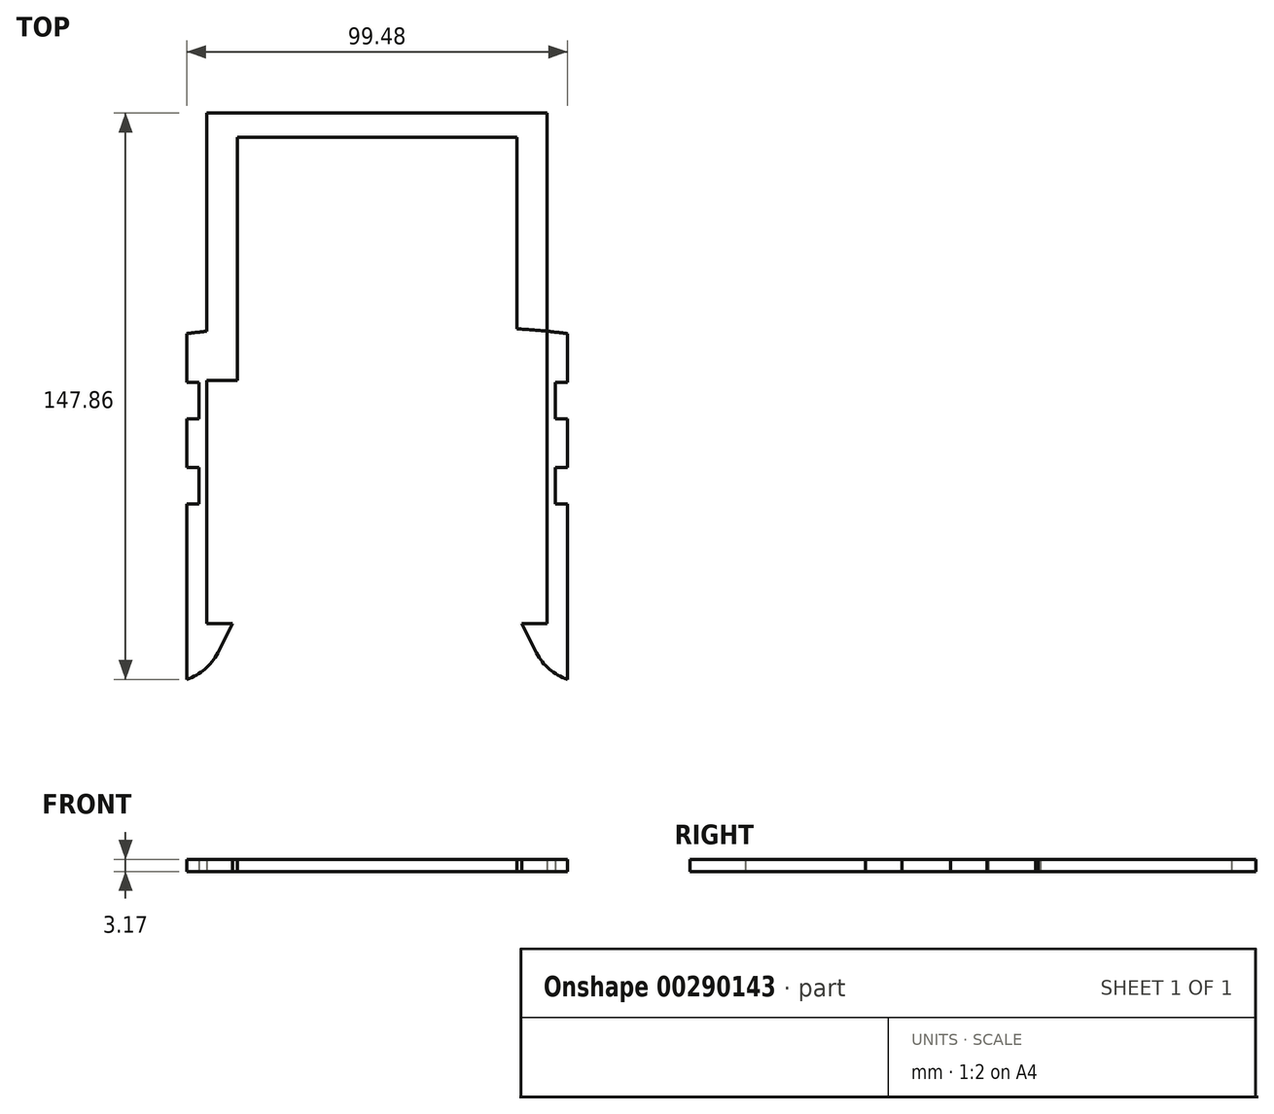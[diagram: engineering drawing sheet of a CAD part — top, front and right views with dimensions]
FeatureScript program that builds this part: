
annotation { "Feature Type Name" : "Feature", "Feature Type Description" : "" }
export const myFeature = defineFeature(function(context is Context, id is Id, definition is map)
    precondition{}
    {
        {
            var Q0;
            Q0=qCreatedBy(makeId("Top.planeOp"),FACE);
            var sketch = newSketch(context, id + "F0", { "sketchPlane" : qUnion([Q0])});
            skLineSegment(sketch, "E0", {"start": v(0, 51.86) * mm, "end": v(-27.09, 51.86) * mm});
            skLineSegment(sketch, "E1", {"start": v(0, -7.34) * mm, "end": v(-21.95, -7.34) * mm});
            skLineSegment(sketch, "E2", {"start": v(-31.65, -13.33) * mm, "end": v(-41.64, -33.02) * mm});
            skArc(sketch, "E3", {"start": v(-21.95, -7.34) * mm, "mid": v(-27.65, -8.97) * mm, "end": v(-31.65, -13.33) * mm});
            skArc(sketch, "E4", {"start": v(-59.94, -39.17) * mm, "mid": v(-49.53, -39.84) * mm, "end": v(-41.64, -33.02) * mm});
            skArc(sketch, "E5", {"start": v(-76.83, -17.66) * mm, "mid": v(-71.66, -30.99) * mm, "end": v(-59.94, -39.17) * mm});
            skArc(sketch, "E6", {"start": v(-58.6, 46.17) * mm, "mid": v(-70.66, 15.1) * mm, "end": v(-76.83, -17.66) * mm});
            skArc(sketch, "E7", {"start": v(-49.74, 50.36) * mm, "mid": v(-54.5, 48.95) * mm, "end": v(-58.6, 46.17) * mm});
            skArc(sketch, "E8", {"start": v(-27.09, 51.86) * mm, "mid": v(-38.44, 51.49) * mm, "end": v(-49.74, 50.36) * mm});
            skArc(sketch, "E9.MirrorCS", {"start": v(27.09, 51.86) * mm, "mid": v(38.44, 51.49) * mm, "end": v(49.74, 50.36) * mm});
            skArc(sketch, "E10.MirrorCS", {"start": v(49.74, 50.36) * mm, "mid": v(54.5, 48.95) * mm, "end": v(58.6, 46.17) * mm});
            skArc(sketch, "E11.MirrorCS", {"start": v(21.95, -7.34) * mm, "mid": v(27.65, -8.97) * mm, "end": v(31.65, -13.33) * mm});
            skLineSegment(sketch, "E12.MirrorCS", {"start": v(0, -7.34) * mm, "end": v(21.95, -7.34) * mm});
            skArc(sketch, "E13.MirrorCS", {"start": v(59.94, -39.17) * mm, "mid": v(49.53, -39.84) * mm, "end": v(41.64, -33.02) * mm});
            skArc(sketch, "E14.MirrorCS", {"start": v(76.83, -17.66) * mm, "mid": v(71.66, -30.99) * mm, "end": v(59.94, -39.17) * mm});
            skArc(sketch, "E15.MirrorCS", {"start": v(58.6, 46.17) * mm, "mid": v(70.66, 15.1) * mm, "end": v(76.83, -17.66) * mm});
            skLineSegment(sketch, "E16.MirrorCS", {"start": v(0, 51.86) * mm, "end": v(27.09, 51.86) * mm});
            skLineSegment(sketch, "E17.MirrorCS", {"start": v(31.65, -13.33) * mm, "end": v(41.64, -33.02) * mm});
            skLineSegment(sketch, "E18.bottom", {"start": v(-36.51, 101.6) * mm, "end": v(36.51, 101.6) * mm});
            skLineSegment(sketch, "E18.top", {"start": v(-36.51, 38.1) * mm, "end": v(36.51, 38.1) * mm});
            skLineSegment(sketch, "E18.left", {"start": v(-36.51, 101.6) * mm, "end": v(-36.51, 38.1) * mm});
            skLineSegment(sketch, "E18.right", {"start": v(36.51, 101.6) * mm, "end": v(36.51, 38.1) * mm});
            skPoint(sketch, "E18.middle", {"position": v(0, 69.85) * mm});
            skLineSegment(sketch, "E19.bottom", {"start": v(-44.45, -25.4) * mm, "end": v(44.45, -25.4) * mm});
            skLineSegment(sketch, "E19.top", {"start": v(-44.45, 38.1) * mm, "end": v(44.45, 38.1) * mm});
            skLineSegment(sketch, "E19.left", {"start": v(-44.45, -25.4) * mm, "end": v(-44.45, 38.1) * mm});
            skLineSegment(sketch, "E19.right", {"start": v(44.45, -25.4) * mm, "end": v(44.45, 38.1) * mm});
            skPoint(sketch, "E19.middle", {"position": v(0, 6.35) * mm});
            skLineSegment(sketch, "E20", {"start": v(-44.45, 38.1) * mm, "end": v(-44.45, 107.95) * mm});
            skLineSegment(sketch, "E21", {"start": v(-44.45, 107.95) * mm, "end": v(44.45, 107.95) * mm});
            skLineSegment(sketch, "E22", {"start": v(44.45, 107.95) * mm, "end": v(44.45, 38.1) * mm});
            skLineSegment(sketch, "E23.bottom", {"start": v(-49.74, 37.66) * mm, "end": v(-46.56, 37.66) * mm});
            skLineSegment(sketch, "E23.top", {"start": v(-49.74, 28.13) * mm, "end": v(-46.56, 28.13) * mm});
            skLineSegment(sketch, "E23.left", {"start": v(-49.74, 37.66) * mm, "end": v(-49.74, 28.13) * mm});
            skLineSegment(sketch, "E23.right", {"start": v(-46.56, 37.66) * mm, "end": v(-46.56, 28.13) * mm});
            skLineSegment(sketch, "E24.bottom", {"start": v(-49.74, 15.43) * mm, "end": v(-46.56, 15.43) * mm});
            skLineSegment(sketch, "E24.top", {"start": v(-49.74, 5.9) * mm, "end": v(-46.56, 5.9) * mm});
            skLineSegment(sketch, "E24.left", {"start": v(-49.74, 15.43) * mm, "end": v(-49.74, 5.9) * mm});
            skLineSegment(sketch, "E25", {"start": v(-46.56, 15.43) * mm, "end": v(-46.56, 5.9) * mm});
            skLineSegment(sketch, "E26.MirrorCS", {"start": v(49.74, 15.43) * mm, "end": v(46.56, 15.43) * mm});
            skLineSegment(sketch, "E27.MirrorCS", {"start": v(49.74, 5.9) * mm, "end": v(46.56, 5.9) * mm});
            skLineSegment(sketch, "E28.MirrorCS", {"start": v(49.74, 37.66) * mm, "end": v(46.56, 37.66) * mm});
            skLineSegment(sketch, "E29.MirrorCS", {"start": v(49.74, 28.13) * mm, "end": v(46.56, 28.13) * mm});
            skLineSegment(sketch, "E30.MirrorCS", {"start": v(49.74, 37.66) * mm, "end": v(49.74, 28.13) * mm});
            skLineSegment(sketch, "E31.MirrorCS", {"start": v(46.56, 37.66) * mm, "end": v(46.56, 28.13) * mm});
            skLineSegment(sketch, "E32.MirrorCS", {"start": v(46.56, 15.43) * mm, "end": v(46.56, 5.9) * mm});
            skLineSegment(sketch, "E33.MirrorCS", {"start": v(49.74, 15.43) * mm, "end": v(49.74, 5.9) * mm});
            skLineSegment(sketch, "E34", {"start": v(-49.74, 50.36) * mm, "end": v(-49.74, -39.9) * mm});
            skLineSegment(sketch, "E35", {"start": v(49.74, 50.36) * mm, "end": v(49.74, -39.9) * mm});
            skSolve(sketch);
        }
        {
            var Q0;
            {var subQ0=sQuery(id+"F0.wireOp",EDGE,"E20");var subQ1=sQuery(id+"F0.wireOp",EDGE,"E8");var subQ2=makeQuery(id+"F0.imprint","INTERSECT",VERTEX,{"derivedFrom":[subQ1,subQ0]});Q0=makeQuery(id+"F0.imprint","IMPRINT",FACE,{"disambiguationData":[TD([[makeQuery(id+"F0.imprint","IMPRINT",EDGE,{"disambiguationData":[TD([[subQ2,1.0]])],"derivedFrom":subQ1}),1.0]])]});}
            var Q1;
            {var subQ0=sQuery(id+"F0.wireOp",EDGE,"E18.bottom");Q1=makeQuery(id+"F0.imprint","IMPRINT",FACE,{"disambiguationData":[TD([[makeQuery(id+"F0.imprint","IMPRINT",EDGE,{"derivedFrom":subQ0}),1.0]])]});}
            var Q2;
            {var subQ0=sQuery(id+"F0.wireOp",EDGE,"E22");var subQ1=sQuery(id+"F0.wireOp",EDGE,"E9.MirrorCS");var subQ2=makeQuery(id+"F0.imprint","INTERSECT",VERTEX,{"derivedFrom":[subQ1,subQ0]});Q2=makeQuery(id+"F0.imprint","IMPRINT",FACE,{"disambiguationData":[TD([[makeQuery(id+"F0.imprint","IMPRINT",EDGE,{"disambiguationData":[TD([[subQ2,1.0]])],"derivedFrom":subQ1}),-1.0]])]});}
            var Q3;
            {var subQ0=sQuery(id+"F0.wireOp",EDGE,"E19.left");Q3=makeQuery(id+"F0.imprint","IMPRINT",FACE,{"disambiguationData":[TD([[makeQuery(id+"F0.imprint","IMPRINT",EDGE,{"derivedFrom":subQ0}),1.0]])]});}
            var Q4;
            {var subQ0=sQuery(id+"F0.wireOp",EDGE,"E19.right");Q4=makeQuery(id+"F0.imprint","IMPRINT",FACE,{"disambiguationData":[TD([[makeQuery(id+"F0.imprint","IMPRINT",EDGE,{"derivedFrom":subQ0}),-1.0]])]});}
            extrude(context, id + "F1", {"entities" : qUnion([Q0, Q1, Q2, Q3, Q4]), "depth" : 3.17 * mm});
        }
    });
